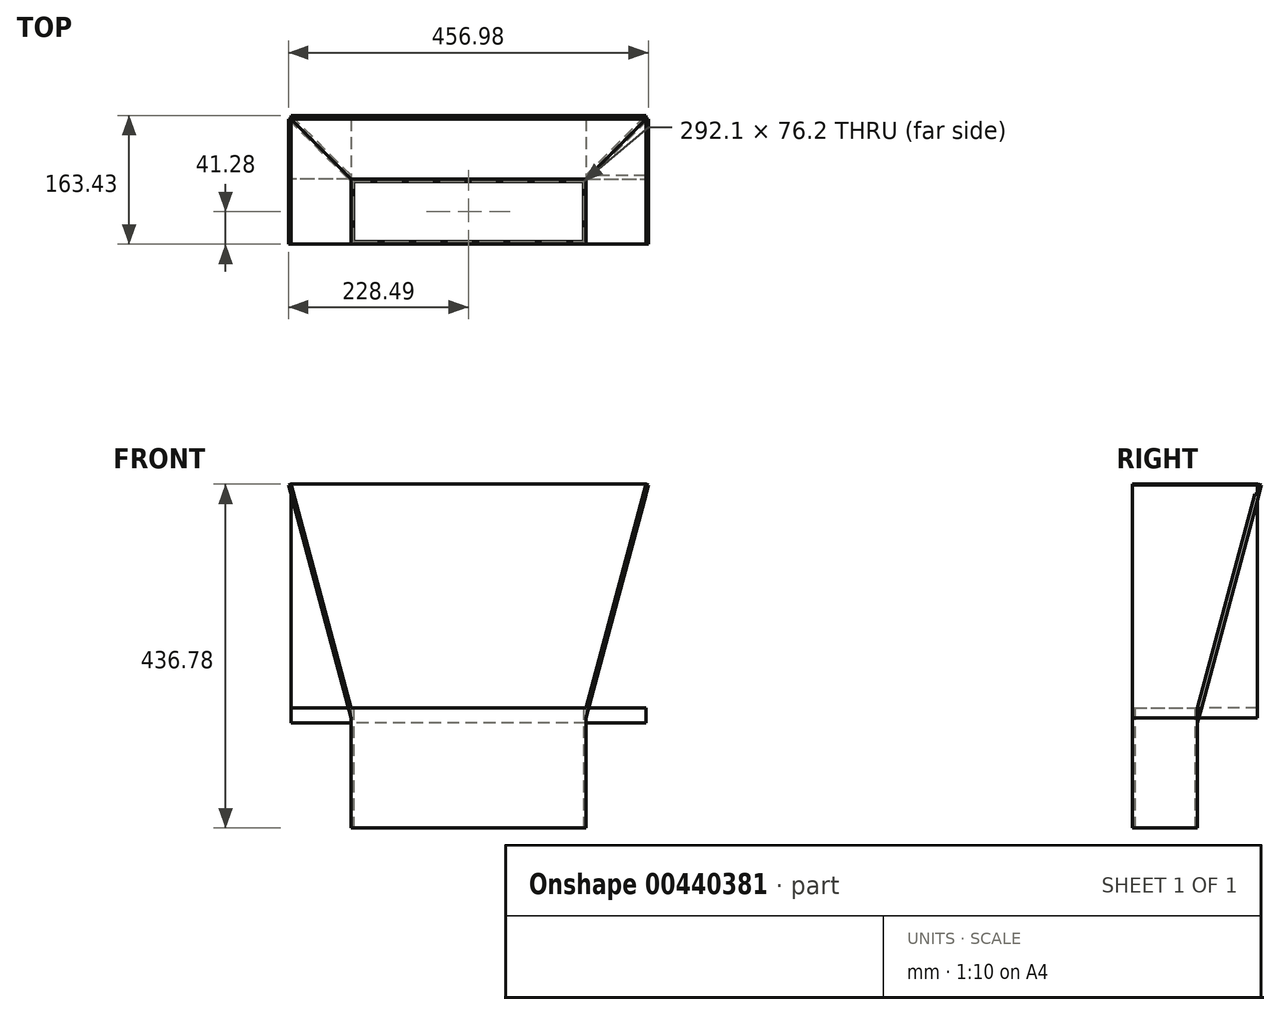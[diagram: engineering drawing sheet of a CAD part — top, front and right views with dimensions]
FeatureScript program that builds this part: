
annotation { "Feature Type Name" : "Feature", "Feature Type Description" : "" }
export const myFeature = defineFeature(function(context is Context, id is Id, definition is map)
    precondition{}
    {
        {
            var Q0;
            Q0=qCreatedBy(makeId("Top.planeOp"),FACE);
            var sketch = newSketch(context, id + "F0", { "sketchPlane" : qUnion([Q0])});
            skLineSegment(sketch, "E0.bottom", {"start": v(146.05, -38.1) * mm, "end": v(-146.05, -38.1) * mm});
            skLineSegment(sketch, "E0.top", {"start": v(146.05, 38.1) * mm, "end": v(-146.05, 38.1) * mm});
            skLineSegment(sketch, "E0.left", {"start": v(146.05, -38.1) * mm, "end": v(146.05, 38.1) * mm});
            skLineSegment(sketch, "E0.right", {"start": v(-146.05, -38.1) * mm, "end": v(-146.05, 38.1) * mm});
            skPoint(sketch, "E0.middle", {"position": v(0, 0) * mm});
            skLineSegment(sketch, "E1.bottom", {"start": v(-149.23, -41.28) * mm, "end": v(149.23, -41.28) * mm});
            skLineSegment(sketch, "E1.top", {"start": v(-149.23, 41.28) * mm, "end": v(149.23, 41.28) * mm});
            skLineSegment(sketch, "E1.left", {"start": v(-149.23, -41.28) * mm, "end": v(-149.23, 41.28) * mm});
            skLineSegment(sketch, "E1.right", {"start": v(149.23, -41.28) * mm, "end": v(149.23, 41.28) * mm});
            skSolve(sketch);
        }
        {
            var Q0;
            Q0=makeQuery(id+"F0.imprint","IMPRINT",FACE,{"disambiguationData":[TD([[makeQuery(id+"F0.imprint","IMPRINT",EDGE,{"derivedFrom":sQuery(id+"F0.wireOp",EDGE,"E0.bottom")}),1.0]])]});
            extrude(context, id + "F1", {"entities" : qUnion([Q0]), "depth" : 152.4 * mm});
        }
        {
            var Q0;
            Q0=makeQuery(id+"F1.opExtrude","SWEPT_FACE",FACE,{"disambiguationData":[OSD([sQuery(id+"F0.wireOp",EDGE,"E1.bottom")])]});
            var sketch = newSketch(context, id + "F2", { "sketchPlane" : qUnion([Q0])});
            skLineSegment(sketch, "E2", {"start": v(-149.23, 152.4) * mm, "end": v(-225.43, 436.78) * mm});
            skLineSegment(sketch, "E3", {"start": v(-225.43, 436.78) * mm, "end": v(-228.5, 435.96) * mm});
            skLineSegment(sketch, "E4", {"start": v(-228.5, 435.96) * mm, "end": v(-149.23, 140.13) * mm});
            skSolve(sketch);
        }
        {
            var Q0;
            Q0=makeQuery(id+"F1.opExtrude","SWEPT_FACE",FACE,{"disambiguationData":[OSD([sQuery(id+"F0.wireOp",EDGE,"E1.left")])]});
            var sketch = newSketch(context, id + "F3", { "sketchPlane" : qUnion([Q0])});
            skLineSegment(sketch, "E5", {"start": v(-41.28, 152.4) * mm, "end": v(-117.48, 436.78) * mm});
            skLineSegment(sketch, "E6", {"start": v(-117.48, 436.78) * mm, "end": v(-122.15, 435.53) * mm});
            skLineSegment(sketch, "E7", {"start": v(-122.15, 435.53) * mm, "end": v(-41.28, 133.7) * mm});
            skSolve(sketch);
        }
        {
            var Q0;
            {var subQ0=sQuery(id+"F2.wireOp",EDGE,"E2");Q0=makeQuery(id+"F2.imprint","IMPRINT",FACE,{"disambiguationData":[TD([[makeQuery(id+"F2.imprint","IMPRINT",EDGE,{"derivedFrom":subQ0}),1.0]])]});}
            extrude(context, id + "F4", {"entities" : qUnion([Q0]), "operationType" : NewBodyOperationType.ADD, "oppositeDirection" : true, "depth" : 158.75 * mm});
        }
        {
            var Q0;
            {var subQ0=sQuery(id+"F3.wireOp",EDGE,"E5");Q0=makeQuery(id+"F3.imprint","IMPRINT",FACE,{"disambiguationData":[TD([[makeQuery(id+"F3.imprint","IMPRINT",EDGE,{"derivedFrom":subQ0}),1.0]])]});}
            extrude(context, id + "F5", {"entities" : qUnion([Q0]), "operationType" : NewBodyOperationType.ADD, "oppositeDirection" : true, "depth" : 254 * mm, "hasSecondDirection" : true, "secondDirectionOppositeDirection" : false, "secondDirectionDepth" : 76.2 * mm});
        }
        {
            var Q0;
            Q0=makeQuery(id+"F1.opExtrude","SWEPT_BODY",BODY,{"disambiguationData":[OSD([sQuery(id+"F0.wireOp",EDGE,"E0.bottom"),sQuery(id+"F0.wireOp",EDGE,"E0.top"),sQuery(id+"F0.wireOp",EDGE,"E0.left"),sQuery(id+"F0.wireOp",EDGE,"E0.right"),sQuery(id+"F0.wireOp",EDGE,"E1.bottom"),sQuery(id+"F0.wireOp",EDGE,"E1.top"),sQuery(id+"F0.wireOp",EDGE,"E1.left"),sQuery(id+"F0.wireOp",EDGE,"E1.right")])]});
            var Q1;
            Q1=qCreatedBy(makeId("Right.planeOp"),FACE);
            mirror(context, id + "F6", {"operationType" : NewBodyOperationType.ADD, "entities" : qUnion([Q0]), "mirrorPlane" : qUnion([Q1])});
        }
        {
            var Q0;
            {var subQ0=sQuery(id+"F3.wireOp",EDGE,"E5");Q0=makeQuery(id+"F6.opPattern","COPY",FACE,{"derivedFrom":makeQuery(id+"F5.boolean.opBoolean","SPLIT",FACE,{"disambiguationData":[TD([makeQuery(id+"F4.opExtrude","SWEPT_FACE",FACE,{"disambiguationData":[OSD([sQuery(id+"F2.wireOp",EDGE,"E4")])]})])],"derivedFrom":makeQuery(id+"F5.opExtrude","SWEPT_FACE",FACE,{"disambiguationData":[OSD([subQ0])]})}),"instanceName":"1"});}
            extrude(context, id + "F7", {"entities" : qUnion([Q0]), "operationType" : NewBodyOperationType.REMOVE, "oppositeDirection" : true, "depth" : 25.4 * mm});
        }
    });
